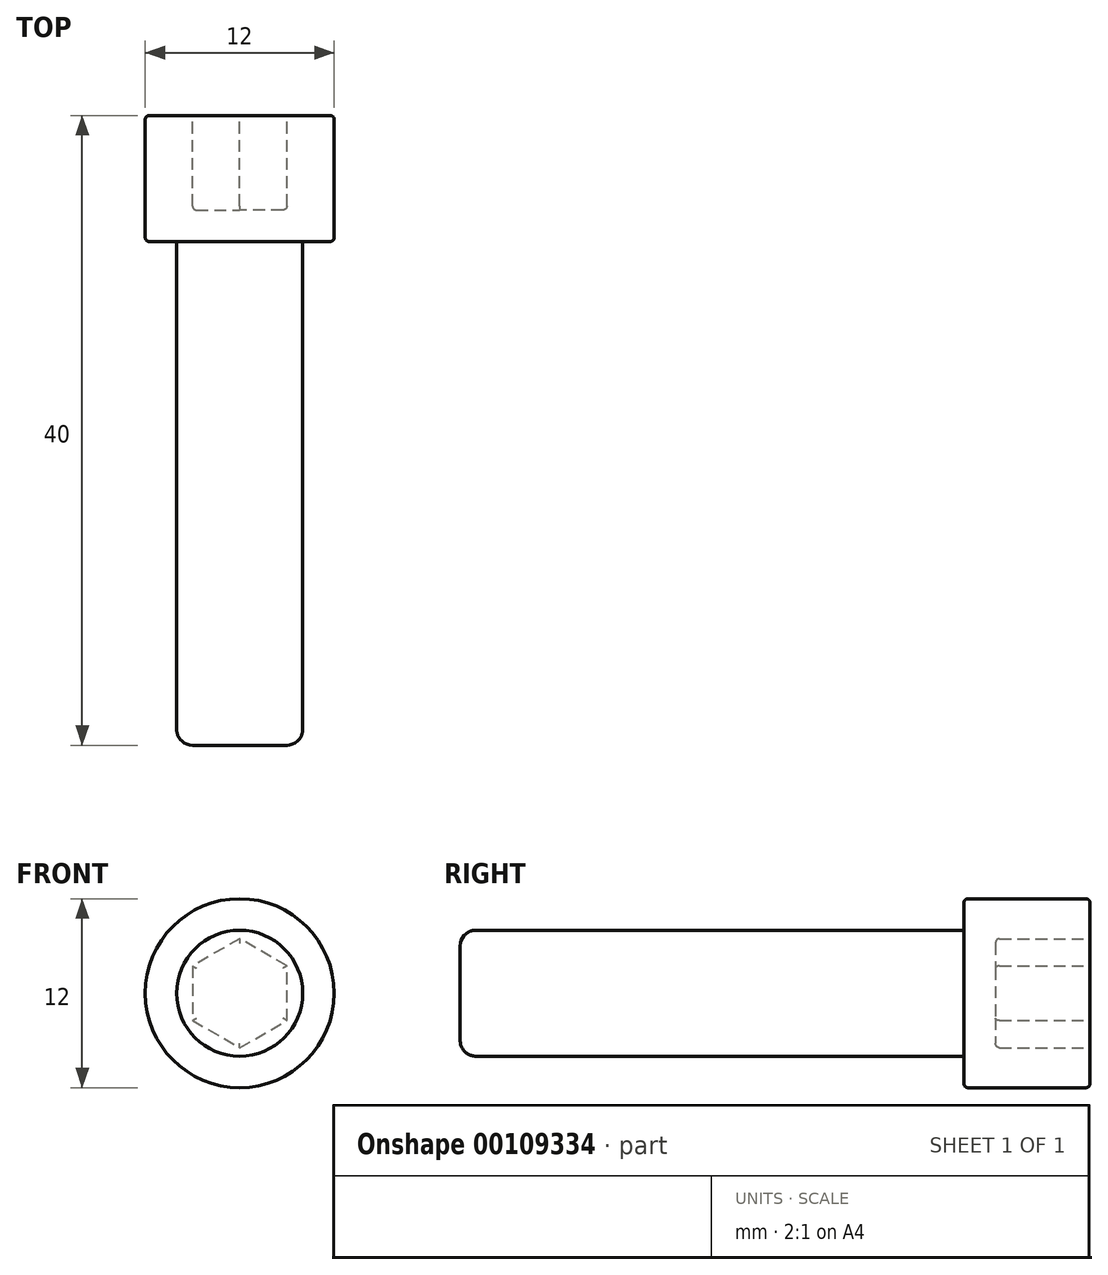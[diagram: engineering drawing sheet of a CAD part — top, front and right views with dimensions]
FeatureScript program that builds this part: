
annotation { "Feature Type Name" : "Feature", "Feature Type Description" : "" }
export const myFeature = defineFeature(function(context is Context, id is Id, definition is map)
    precondition{}
    {
        {
            var Q0;
            Q0=qCreatedBy(makeId("Front.planeOp"),FACE);
            var sketch = newSketch(context, id + "F0", { "sketchPlane" : qUnion([Q0])});
            skCircle(sketch, "E0", {"center": v(0, 0) * mm, "radius": 4 * mm});
            skCircle(sketch, "E1", {"center": v(0, 0) * mm, "radius": 6 * mm});
            skSolve(sketch);
        }
        {
            var Q0;
            Q0=makeQuery(id+"F0.imprint","IMPRINT",FACE,{"disambiguationData":[TD([[makeQuery(id+"F0.imprint","IMPRINT",EDGE,{"derivedFrom":sQuery(id+"F0.wireOp",EDGE,"E0")}),1.0]])]});
            extrude(context, id + "F1", {"entities" : qUnion([Q0]), "depth" : 32 * mm});
        }
        {
            var Q0;
            Q0=makeQuery(id+"F0.imprint","IMPRINT",FACE,{"disambiguationData":[TD([[makeQuery(id+"F0.imprint","IMPRINT",EDGE,{"derivedFrom":sQuery(id+"F0.wireOp",EDGE,"E0")}),-1.0]])]});
            var Q1;
            Q1=makeQuery(id+"F0.imprint","IMPRINT",FACE,{"disambiguationData":[TD([[makeQuery(id+"F0.imprint","IMPRINT",EDGE,{"derivedFrom":sQuery(id+"F0.wireOp",EDGE,"E0")}),1.0]])]});
            extrude(context, id + "F2", {"entities" : qUnion([Q0, Q1]), "operationType" : NewBodyOperationType.ADD, "oppositeDirection" : true, "depth" : 8 * mm});
        }
        {
            var Q0;
            Q0=makeQuery(id+"F2.opExtrude","CAP_FACE",FACE,{"disambiguationData":[OSD([sQuery(id+"F0.wireOp",EDGE,"E1")])],"isStart":false});
            var sketch = newSketch(context, id + "F3", { "sketchPlane" : qUnion([Q0])});
            skCircle(sketch, "E2.cCircle", {"center": v(0, 0) * mm, "radius": 3 * mm, "construction": true});
            skLineSegment(sketch, "E2.0", {"start": v(-3, -1.73) * mm, "end": v(-3, 1.73) * mm});
            skLineSegment(sketch, "E2.1", {"start": v(-3, 1.73) * mm, "end": v(0, 3.46) * mm});
            skLineSegment(sketch, "E2.2", {"start": v(0, 3.46) * mm, "end": v(3, 1.73) * mm});
            skLineSegment(sketch, "E2.3", {"start": v(3, 1.73) * mm, "end": v(3, -1.73) * mm});
            skLineSegment(sketch, "E2.4", {"start": v(3, -1.73) * mm, "end": v(0, -3.46) * mm});
            skLineSegment(sketch, "E2.5", {"start": v(0, -3.46) * mm, "end": v(-3, -1.73) * mm});
            skPoint(sketch, "E2.0.midPoint", {"position": v(-3, 0) * mm});
            skSolve(sketch);
        }
        {
            var Q0;
            Q0=makeQuery(id+"F3.imprint","IMPRINT",FACE,{"disambiguationData":[TD([[makeQuery(id+"F3.imprint","IMPRINT",EDGE,{"derivedFrom":sQuery(id+"F3.wireOp",EDGE,"E2.0")}),-1.0]])]});
            extrude(context, id + "F4", {"entities" : qUnion([Q0]), "operationType" : NewBodyOperationType.REMOVE, "oppositeDirection" : true, "depth" : 6 * mm});
        }
        {
            var Q0;
            Q0=makeQuery(id+"F4.boolean.opBoolean","COPY",EDGE,{"derivedFrom":makeQuery(id+"F4.opExtrude","CAP_EDGE",EDGE,{"disambiguationData":[OSD([sQuery(id+"F3.wireOp",EDGE,"E2.5")])],"isStart":true})});
            var Q1;
            Q1=makeQuery(id+"F4.boolean.opBoolean","COPY",EDGE,{"derivedFrom":makeQuery(id+"F4.opExtrude","CAP_EDGE",EDGE,{"disambiguationData":[OSD([sQuery(id+"F3.wireOp",EDGE,"E2.4")])],"isStart":true})});
            var Q2;
            Q2=makeQuery(id+"F4.boolean.opBoolean","COPY",EDGE,{"derivedFrom":makeQuery(id+"F4.opExtrude","CAP_EDGE",EDGE,{"disambiguationData":[OSD([sQuery(id+"F3.wireOp",EDGE,"E2.3")])],"isStart":true})});
            var Q3;
            Q3=makeQuery(id+"F4.boolean.opBoolean","COPY",EDGE,{"derivedFrom":makeQuery(id+"F4.opExtrude","CAP_EDGE",EDGE,{"disambiguationData":[OSD([sQuery(id+"F3.wireOp",EDGE,"E2.2")])],"isStart":true})});
            var Q4;
            Q4=makeQuery(id+"F4.boolean.opBoolean","COPY",EDGE,{"derivedFrom":makeQuery(id+"F4.opExtrude","CAP_EDGE",EDGE,{"disambiguationData":[OSD([sQuery(id+"F3.wireOp",EDGE,"E2.1")])],"isStart":true})});
            var Q5;
            Q5=makeQuery(id+"F4.boolean.opBoolean","COPY",EDGE,{"derivedFrom":makeQuery(id+"F4.opExtrude","CAP_EDGE",EDGE,{"disambiguationData":[OSD([sQuery(id+"F3.wireOp",EDGE,"E2.0")])],"isStart":true})});
            var Q6;
            Q6=makeQuery(id+"F2.opExtrude","CAP_EDGE",EDGE,{"disambiguationData":[OSD([sQuery(id+"F0.wireOp",EDGE,"E1")])],"isStart":false});
            var Q7;
            Q7=makeQuery(id+"F4.boolean.opBoolean","COPY",EDGE,{"derivedFrom":makeQuery(id+"F4.opExtrude","CAP_EDGE",EDGE,{"disambiguationData":[OSD([sQuery(id+"F3.wireOp",EDGE,"E2.5")])],"isStart":false})});
            var Q8;
            Q8=makeQuery(id+"F4.boolean.opBoolean","COPY",EDGE,{"derivedFrom":makeQuery(id+"F4.opExtrude","CAP_EDGE",EDGE,{"disambiguationData":[OSD([sQuery(id+"F3.wireOp",EDGE,"E2.4")])],"isStart":false})});
            var Q9;
            Q9=makeQuery(id+"F4.boolean.opBoolean","COPY",EDGE,{"derivedFrom":makeQuery(id+"F4.opExtrude","CAP_EDGE",EDGE,{"disambiguationData":[OSD([sQuery(id+"F3.wireOp",EDGE,"E2.0")])],"isStart":false})});
            var Q10;
            Q10=makeQuery(id+"F4.boolean.opBoolean","COPY",EDGE,{"derivedFrom":makeQuery(id+"F4.opExtrude","CAP_EDGE",EDGE,{"disambiguationData":[OSD([sQuery(id+"F3.wireOp",EDGE,"E2.1")])],"isStart":false})});
            var Q11;
            Q11=makeQuery(id+"F4.boolean.opBoolean","COPY",EDGE,{"derivedFrom":makeQuery(id+"F4.opExtrude","CAP_EDGE",EDGE,{"disambiguationData":[OSD([sQuery(id+"F3.wireOp",EDGE,"E2.2")])],"isStart":false})});
            var Q12;
            Q12=makeQuery(id+"F4.boolean.opBoolean","COPY",EDGE,{"derivedFrom":makeQuery(id+"F4.opExtrude","CAP_EDGE",EDGE,{"disambiguationData":[OSD([sQuery(id+"F3.wireOp",EDGE,"E2.3")])],"isStart":false})});
            var Q13;
            Q13=makeQuery(id+"F2.opExtrude","CAP_EDGE",EDGE,{"disambiguationData":[OSD([sQuery(id+"F0.wireOp",EDGE,"E1")])],"isStart":true});
            fillet(context, id + "F5", {"entities" : qUnion([Q0, Q1, Q2, Q3, Q4, Q5, Q6, Q7, Q8, Q9, Q10, Q11, Q12, Q13]), "radius" : .25 * mm, "tangentPropagation" : true, "allowEdgeOverflow" : false});
        }
        {
            var Q0;
            Q0=makeQuery(id+"F1.opExtrude","CAP_EDGE",EDGE,{"disambiguationData":[OSD([sQuery(id+"F0.wireOp",EDGE,"E0")])],"isStart":false});
            fillet(context, id + "F6", {"entities" : qUnion([Q0]), "radius" : 1 * mm, "tangentPropagation" : true, "allowEdgeOverflow" : false});
        }
    });
